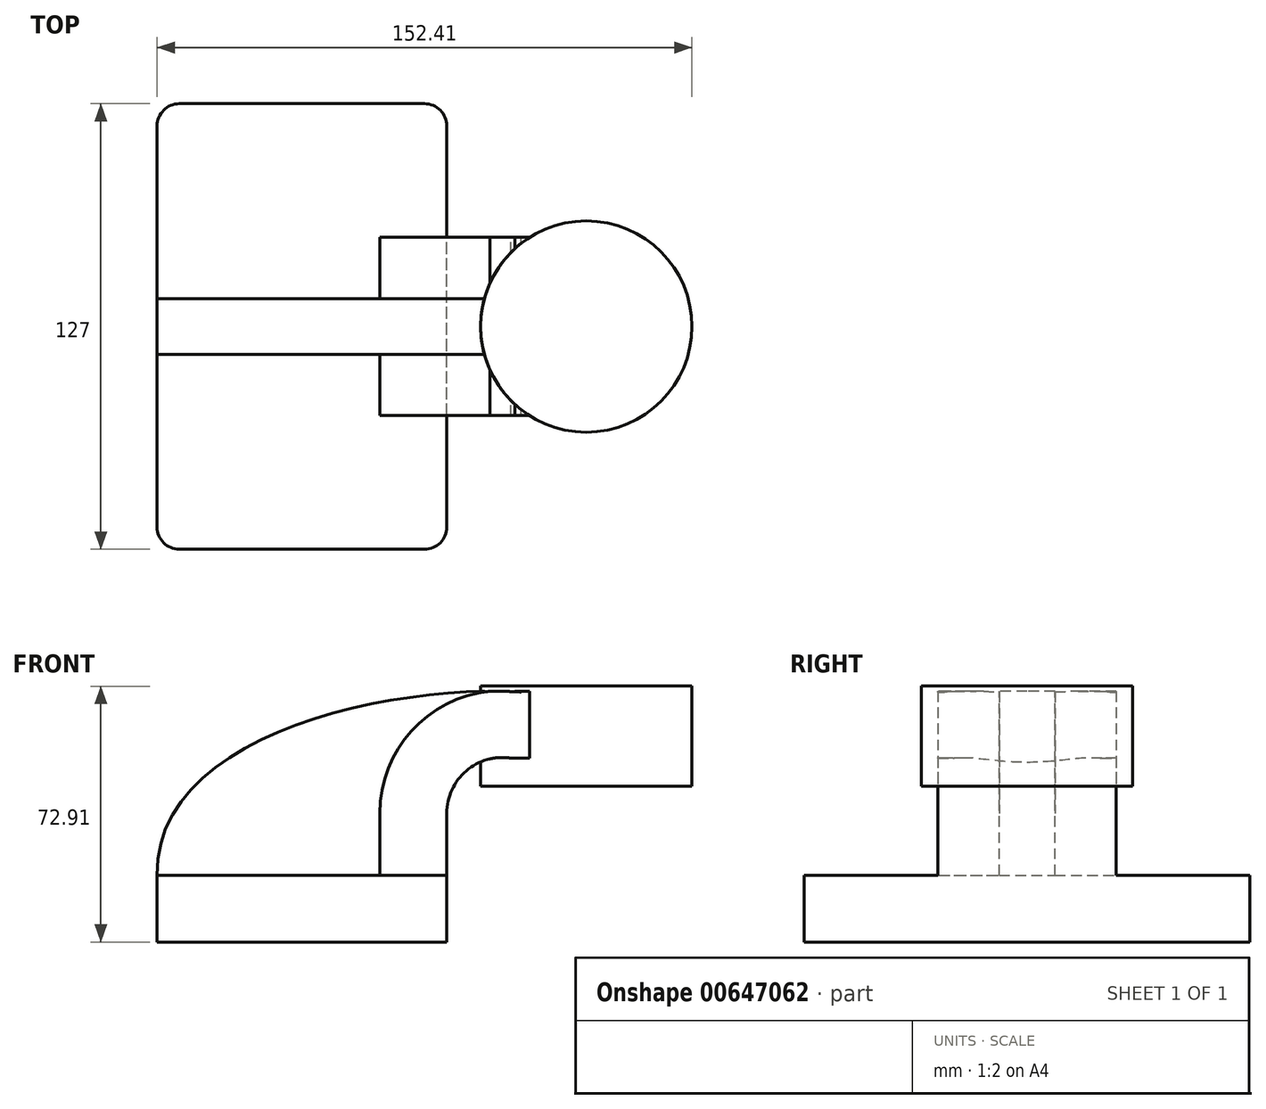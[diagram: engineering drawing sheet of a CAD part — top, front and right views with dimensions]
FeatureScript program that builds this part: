
annotation { "Feature Type Name" : "Feature", "Feature Type Description" : "" }
export const myFeature = defineFeature(function(context is Context, id is Id, definition is map)
    precondition{}
    {
        {
            var Q0;
            Q0=qCreatedBy(makeId("Front.planeOp"),FACE);
            var sketch = newSketch(context, id + "F0", { "sketchPlane" : qUnion([Q0])});
            skLineSegment(sketch, "E0.bottom", {"start": v(-41.28, 9.52) * mm, "end": v(41.28, 9.53) * mm});
            skLineSegment(sketch, "E0.top", {"start": v(-41.28, -9.53) * mm, "end": v(41.28, -9.53) * mm});
            skLineSegment(sketch, "E0.left", {"start": v(-41.28, 9.52) * mm, "end": v(-41.28, -9.53) * mm});
            skLineSegment(sketch, "E0.right", {"start": v(41.28, 9.53) * mm, "end": v(41.28, -9.52) * mm});
            skPoint(sketch, "E0.middle", {"position": v(0, 0) * mm});
            skLineSegment(sketch, "E1", {"start": v(41.28, 9.53) * mm, "end": v(41.28, 27.18) * mm});
            skLineSegment(sketch, "E2.bottom", {"start": v(111.12, 34.8) * mm, "end": v(60.33, 34.8) * mm});
            skLineSegment(sketch, "E2.top", {"start": v(111.12, 63.38) * mm, "end": v(60.33, 63.38) * mm});
            skLineSegment(sketch, "E2.left", {"start": v(111.12, 34.8) * mm, "end": v(111.12, 63.38) * mm});
            skLineSegment(sketch, "E2.right", {"start": v(60.33, 34.8) * mm, "end": v(60.33, 63.38) * mm});
            skPoint(sketch, "E2.middle", {"position": v(85.72, 49.1) * mm});
            skArc(sketch, "E3", {"start": v(41.27, 27.18) * mm, "mid": v(46.8, 39.22) * mm, "end": v(59.55, 42.88) * mm});
            skLineSegment(sketch, "E4", {"start": v(59.55, 42.88) * mm, "end": v(81.02, 42.88) * mm});
            skArc(sketch, "E5.0", {"start": v(22.22, 27.18) * mm, "mid": v(34.4, 53.68) * mm, "end": v(62.42, 61.7) * mm});
            skLineSegment(sketch, "E5.1", {"start": v(22.22, 9.53) * mm, "end": v(22.22, 27.18) * mm});
            skLineSegment(sketch, "E6.0", {"start": v(59.55, 61.93) * mm, "end": v(81.02, 61.93) * mm});
            skLineSegment(sketch, "E7", {"start": v(81.02, 34.8) * mm, "end": v(81.02, 63.38) * mm});
            skFitSpline(sketch, "E8", {"points": [v(-41.28, 9.52) * mm, v(62.42, 61.7) * mm], "startDerivative": vector(-2.3, 120.2) * mm, "endDerivative": vector(113.13, -6.67) * mm});
            skSolve(sketch);
        }
        {
            var Q0;
            Q0=makeQuery(id+"F0.imprint","IMPRINT",FACE,{"disambiguationData":[TD([[makeQuery(id+"F0.imprint","IMPRINT",EDGE,{"derivedFrom":sQuery(id+"F0.wireOp",EDGE,"E0.top")}),1.0]])]});
            extrude(context, id + "F1", {"entities" : qUnion([Q0]), "endBound" : BoundingType.SYMMETRIC, "depth" : 127 * mm, "offsetDistance" : 25.4 * mm});
        }
        {
            var Q0;
            {var subQ5=sQuery(id+"F0.wireOp",EDGE,"E1");Q0=makeQuery(id+"F0.imprint","IMPRINT",FACE,{"disambiguationData":[TD([[makeQuery(id+"F0.imprint","IMPRINT",EDGE,{"derivedFrom":subQ5}),1.0]])]});}
            var Q1;
            {var subQ5=sQuery(id+"F0.wireOp",EDGE,"E4");var subQ7=sQuery(id+"F0.wireOp",EDGE,"E2.right");var subQ8=makeQuery(id+"F0.imprint","INTERSECT",VERTEX,{"derivedFrom":[subQ7,subQ5]});Q1=makeQuery(id+"F0.imprint","IMPRINT",FACE,{"disambiguationData":[TD([[makeQuery(id+"F0.imprint","IMPRINT",EDGE,{"disambiguationData":[TD([[subQ8,-1.0]])],"derivedFrom":subQ7}),-1.0]])]});}
            extrude(context, id + "F2", {"entities" : qUnion([Q0, Q1]), "operationType" : NewBodyOperationType.ADD, "endBound" : BoundingType.SYMMETRIC, "depth" : 50.8 * mm, "offsetDistance" : 25.4 * mm});
        }
        {
            var Q0;
            {var subQ3=sQuery(id+"F0.wireOp",EDGE,"E5.1");Q0=makeQuery(id+"F0.imprint","IMPRINT",FACE,{"disambiguationData":[TD([[makeQuery(id+"F0.imprint","IMPRINT",EDGE,{"derivedFrom":subQ3}),1.0]])]});}
            extrude(context, id + "F3", {"entities" : qUnion([Q0]), "operationType" : NewBodyOperationType.ADD, "endBound" : BoundingType.SYMMETRIC, "depth" : 15.88 * mm, "offsetDistance" : 25.4 * mm});
        }
        {
            var Q0;
            {var subQ0=sQuery(id+"F0.wireOp",EDGE,"E2.left");Q0=makeQuery(id+"F0.imprint","IMPRINT",FACE,{"disambiguationData":[TD([[makeQuery(id+"F0.imprint","IMPRINT",EDGE,{"derivedFrom":subQ0}),1.0]])]});}
            var Q1;
            Q1=sQuery(id+"F0.wireOp",EDGE,"E7");
            revolve(context, id + "F4", {"operationType" : NewBodyOperationType.ADD, "entities" : qUnion([Q0]), "axis" : qUnion([Q1]), "revolveType" : RevolveType.FULL});
        }
        {
            var Q0;
            Q0=makeQuery(id+"F1.opExtrude","CAP_EDGE",EDGE,{"disambiguationData":[OSD([sQuery(id+"F0.wireOp",EDGE,"E0.left")])],"isStart":false});
            var Q1;
            Q1=makeQuery(id+"F1.opExtrude","CAP_EDGE",EDGE,{"disambiguationData":[OSD([sQuery(id+"F0.wireOp",EDGE,"E0.right")])],"isStart":false});
            var Q2;
            Q2=makeQuery(id+"F1.opExtrude","CAP_EDGE",EDGE,{"disambiguationData":[OSD([sQuery(id+"F0.wireOp",EDGE,"E0.right")])],"isStart":true});
            var Q3;
            Q3=makeQuery(id+"F1.opExtrude","CAP_EDGE",EDGE,{"disambiguationData":[OSD([sQuery(id+"F0.wireOp",EDGE,"E0.left")])],"isStart":true});
            fillet(context, id + "F5", {"entities" : qUnion([Q0, Q1, Q2, Q3]), "radius" : 6.35 * mm, "tangentPropagation" : true, "allowEdgeOverflow" : false});
        }
    });
